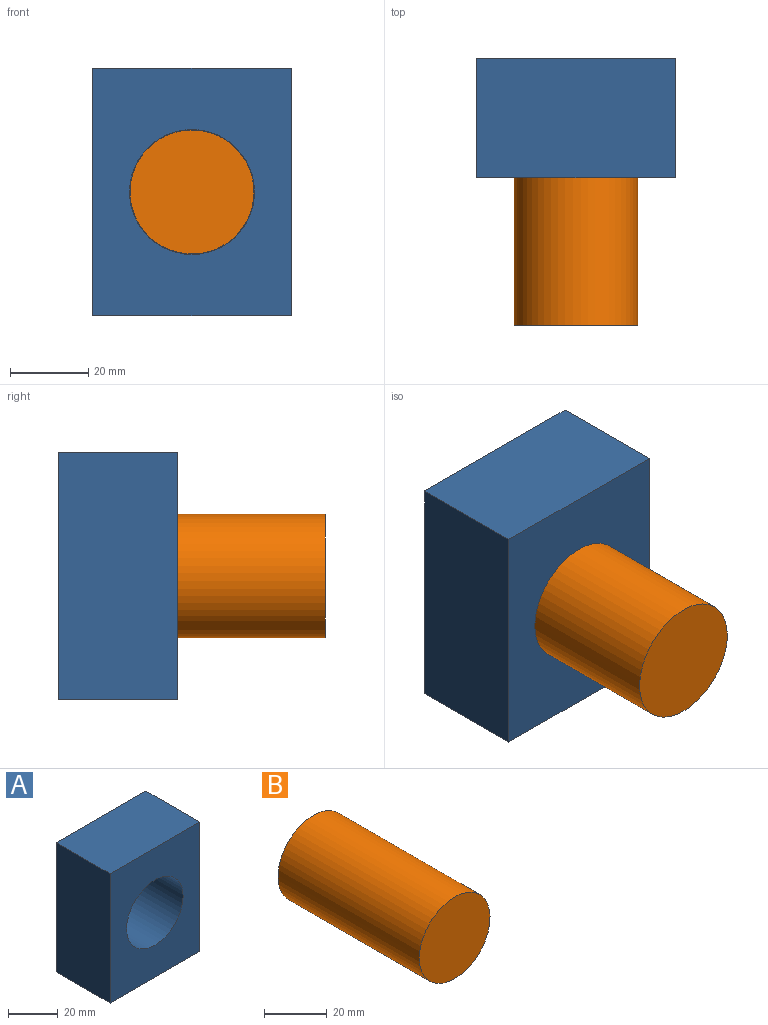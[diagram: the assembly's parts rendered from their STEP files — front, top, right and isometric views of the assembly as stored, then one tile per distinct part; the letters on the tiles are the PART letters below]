
ASSEMBLY  parts=2 mates=1
PART A: 7 faces, bbox 50.8x30.5x63.5 mm
  f0: plane 63.5x30.48mm, normal (-1,0,0), area 1935.5mm2, adj f1,f3,f4,f5
  f1: plane 50.8x30.48mm, normal (0,0,-1), area 1548.4mm2, adj f0,f2,f4,f5
  f2: plane 63.5x30.48mm, normal (1,0,0), area 1935.5mm2, adj f1,f3,f4,f5
  f3: plane 50.8x30.48mm, normal (0,0,1), area 1548.4mm2, adj f0,f2,f4,f5
  f4: plane 63.5x50.8mm, normal (0,-1,0), area 2421.4mm2, adj f0,f1,f2,f3,f6
  f5: plane 63.5x50.8mm, normal (0,1,0), area 2421.4mm2, adj f0,f1,f2,f3,f6
  f6: cylinder r=16mm len=32mm, axis (0,-1,0), area 3064.6mm2, adj f4,f5
PART B: 3 faces, bbox 31.8x63.5x31.8 mm
  f0: cylinder r=15.88mm len=63.5mm, axis (0,1,0), area 6333.8mm2, adj f1,f2
  f1: plane 31.75x31.75mm, normal (0,-1,0), area 791.7mm2, adj f0
  f2: plane 31.75x31.75mm, normal (0,1,0), area 791.7mm2, adj f0
PLACE A t=(0,15.24,0)mm
PLACE B rot(axis=(0,-1,0),69.9deg) t=(46.5,2.83,-3.01)mm
MATE cylindrical B.f0 <-> A.f6  axis (0,1,0) through (25.4,-6.06,31.75)mm
